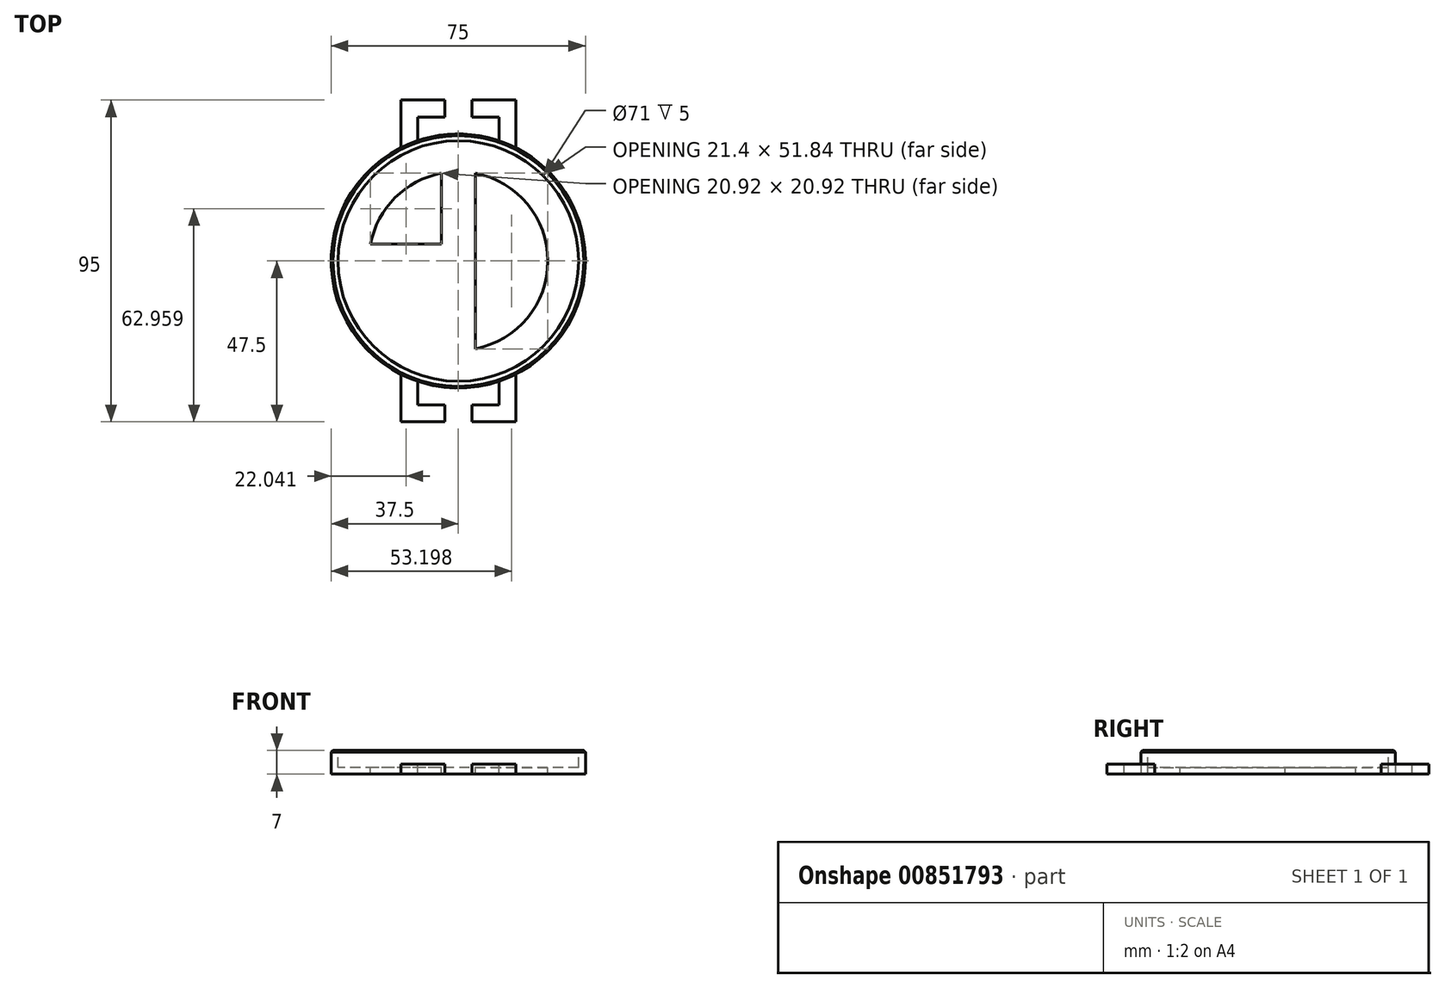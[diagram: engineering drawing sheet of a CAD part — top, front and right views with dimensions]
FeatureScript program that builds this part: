
annotation { "Feature Type Name" : "Feature", "Feature Type Description" : "" }
export const myFeature = defineFeature(function(context is Context, id is Id, definition is map)
    precondition{}
    {
        {
            var Q0;
            Q0=qCreatedBy(makeId("Top.planeOp"),FACE);
            var sketch = newSketch(context, id + "F0", { "sketchPlane" : qUnion([Q0])});
            skCircle(sketch, "E0", {"center": v(0, 0) * mm, "radius": 37.5 * mm});
            skSolve(sketch);
        }
        {
            var Q0;
            Q0=makeQuery(id+"F0.imprint","IMPRINT",FACE,{"disambiguationData":[TD([[makeQuery(id+"F0.imprint","IMPRINT",EDGE,{"derivedFrom":sQuery(id+"F0.wireOp",EDGE,"E0")}),1.0]])]});
            extrude(context, id + "F1", {"entities" : qUnion([Q0]), "depth" : 7 * mm, "offsetDistance" : 25 * mm});
        }
        {
            var Q0;
            Q0=makeQuery(id+"F1.opExtrude","CAP_FACE",FACE,{"disambiguationData":[OSD([sQuery(id+"F0.wireOp",EDGE,"E0")])],"isStart":false});
            var sketch = newSketch(context, id + "F2", { "sketchPlane" : qUnion([Q0])});
            skCircle(sketch, "E1", {"center": v(0, 0) * mm, "radius": 35.5 * mm});
            skSolve(sketch);
        }
        {
            var Q0;
            Q0=makeQuery(id+"F2.imprint","IMPRINT",FACE,{"disambiguationData":[TD([[makeQuery(id+"F2.imprint","IMPRINT",EDGE,{"derivedFrom":sQuery(id+"F2.wireOp",EDGE,"E1")}),1.0]])]});
            extrude(context, id + "F3", {"entities" : qUnion([Q0]), "operationType" : NewBodyOperationType.REMOVE, "oppositeDirection" : true, "depth" : 5 * mm, "offsetDistance" : 25 * mm});
        }
        {
            var Q0;
            Q0=makeQuery(id+"F1.opExtrude","CAP_EDGE",EDGE,{"disambiguationData":[OSD([sQuery(id+"F0.wireOp",EDGE,"E0")])],"isStart":false});
            chamfer(context, id + "F4", {"entities" : qUnion([Q0]), "width" : .5 * mm, "tangentPropagation" : true});
        }
        {
            var Q0;
            Q0=makeQuery(id+"F1.opExtrude","CAP_FACE",FACE,{"disambiguationData":[OSD([sQuery(id+"F0.wireOp",EDGE,"E0")])],"isStart":true});
            var sketch = newSketch(context, id + "F5", { "sketchPlane" : qUnion([Q0])});
            skLineSegment(sketch, "E2", {"start": v(0, 0) * mm, "end": v(0, -47.5) * mm});
            skLineSegment(sketch, "E3", {"start": v(0, 0) * mm, "end": v(0, 47.5) * mm});
            skLineSegment(sketch, "E4", {"start": v(0, 47.5) * mm, "end": v(17, 47.5) * mm});
            skLineSegment(sketch, "E5", {"start": v(0, -47.5) * mm, "end": v(17, -47.5) * mm});
            skLineSegment(sketch, "E6", {"start": v(17, -47.5) * mm, "end": v(17, 47.5) * mm});
            skLineSegment(sketch, "E7", {"start": v(0, 47.5) * mm, "end": v(-17, 47.5) * mm});
            skLineSegment(sketch, "E8", {"start": v(0, -47.5) * mm, "end": v(-17, -47.5) * mm});
            skLineSegment(sketch, "E9", {"start": v(-17, -47.5) * mm, "end": v(-17, 47.5) * mm});
            skSolve(sketch);
        }
        {
            var Q0;
            {var subQ0=sQuery(id+"F5.wireOp",EDGE,"E7");Q0=makeQuery(id+"F5.imprint","IMPRINT",FACE,{"disambiguationData":[TD([[makeQuery(id+"F5.imprint","IMPRINT",EDGE,{"derivedFrom":subQ0}),1.0]])]});}
            var Q1;
            {var subQ0=sQuery(id+"F5.wireOp",EDGE,"E4");Q1=makeQuery(id+"F5.imprint","IMPRINT",FACE,{"disambiguationData":[TD([[makeQuery(id+"F5.imprint","IMPRINT",EDGE,{"derivedFrom":subQ0}),-1.0]])]});}
            var Q2;
            {var subQ0=sQuery(id+"F5.wireOp",EDGE,"E8");Q2=makeQuery(id+"F5.imprint","IMPRINT",FACE,{"disambiguationData":[TD([[makeQuery(id+"F5.imprint","IMPRINT",EDGE,{"derivedFrom":subQ0}),-1.0]])]});}
            var Q3;
            {var subQ0=sQuery(id+"F5.wireOp",EDGE,"E5");Q3=makeQuery(id+"F5.imprint","IMPRINT",FACE,{"disambiguationData":[TD([[makeQuery(id+"F5.imprint","IMPRINT",EDGE,{"derivedFrom":subQ0}),1.0]])]});}
            extrude(context, id + "F6", {"entities" : qUnion([Q0, Q1, Q2, Q3]), "operationType" : NewBodyOperationType.ADD, "depth" : -3 * mm, "offsetDistance" : 25 * mm});
        }
        {
            var Q0;
            Q0=makeQuery(id+"F6.opExtrude","CAP_FACE",FACE,{"disambiguationData":[OSD([sQuery(id+"F0.wireOp",EDGE,"E0"),sQuery(id+"F5.wireOp",EDGE,"E5"),sQuery(id+"F5.wireOp",EDGE,"E6"),sQuery(id+"F5.wireOp",EDGE,"E8"),sQuery(id+"F5.wireOp",EDGE,"E9")])],"isStart":false});
            var sketch = newSketch(context, id + "F7", { "sketchPlane" : qUnion([Q0])});
            skLineSegment(sketch, "E10", {"start": v(0, 47.5) * mm, "end": v(0, 42.5) * mm});
            skLineSegment(sketch, "E11", {"start": v(0, 42.5) * mm, "end": v(17, 42.5) * mm});
            skLineSegment(sketch, "E12", {"start": v(17, 42.5) * mm, "end": v(12, 42.5) * mm});
            skLineSegment(sketch, "E13", {"start": v(12, 42.5) * mm, "end": v(12, 35.53) * mm});
            skLineSegment(sketch, "E14", {"start": v(0, 42.5) * mm, "end": v(-17, 42.5) * mm});
            skLineSegment(sketch, "E15", {"start": v(-17, 42.5) * mm, "end": v(-12, 42.5) * mm});
            skLineSegment(sketch, "E16", {"start": v(-12, 42.5) * mm, "end": v(-12, 35.53) * mm});
            skLineSegment(sketch, "E17", {"start": v(0, 42.5) * mm, "end": v(-4, 42.5) * mm});
            skLineSegment(sketch, "E18", {"start": v(-4, 42.5) * mm, "end": v(4, 42.5) * mm});
            skLineSegment(sketch, "E19", {"start": v(4, 42.5) * mm, "end": v(4, 47.5) * mm});
            skLineSegment(sketch, "E20", {"start": v(-4, 42.5) * mm, "end": v(-4, 47.5) * mm});
            skSolve(sketch);
        }
        {
            var Q0;
            {var subQ3=sQuery(id+"F7.wireOp",EDGE,"E11");Q0=makeQuery(id+"F7.imprint","IMPRINT",FACE,{"disambiguationData":[TD([[makeQuery(id+"F7.imprint","IMPRINT",EDGE,{"derivedFrom":subQ3}),-1.0]])]});}
            var Q1;
            {var subQ0=sQuery(id+"F7.wireOp",EDGE,"E10");Q1=makeQuery(id+"F7.imprint","IMPRINT",FACE,{"disambiguationData":[TD([[makeQuery(id+"F7.imprint","IMPRINT",EDGE,{"derivedFrom":subQ0}),1.0]])]});}
            var Q2;
            {var subQ0=sQuery(id+"F7.wireOp",EDGE,"E10");Q2=makeQuery(id+"F7.imprint","IMPRINT",FACE,{"disambiguationData":[TD([[makeQuery(id+"F7.imprint","IMPRINT",EDGE,{"derivedFrom":subQ0}),-1.0]])]});}
            var Q3;
            {var subQ0=sQuery(id+"F5.wireOp",EDGE,"E9");var subQ1=sQuery(id+"F5.wireOp",EDGE,"E6");var subQ2=sQuery(id+"F0.wireOp",EDGE,"E0");Q3=makeQuery(id+"F6.boolean.opBoolean","MERGE",FACE,{"derivedFrom":[makeQuery(id+"F1.opExtrude","CAP_FACE",FACE,{"disambiguationData":[OSD([subQ2])],"isStart":true}),makeQuery(id+"F6.opExtrude","CAP_FACE",FACE,{"disambiguationData":[OSD([subQ2,sQuery(id+"F5.wireOp",EDGE,"E4"),subQ1,sQuery(id+"F5.wireOp",EDGE,"E7"),subQ0])],"isStart":true}),makeQuery(id+"F6.opExtrude","CAP_FACE",FACE,{"disambiguationData":[OSD([subQ2,sQuery(id+"F5.wireOp",EDGE,"E5"),subQ1,sQuery(id+"F5.wireOp",EDGE,"E8"),subQ0])],"isStart":true})]});}
            extrude(context, id + "F8", {"entities" : qUnion([Q0, Q1, Q2]), "operationType" : NewBodyOperationType.REMOVE, "endBound" : BoundingType.UP_TO_SURFACE, "oppositeDirection" : true, "depth" : 25 * mm, "endBoundEntityFace" : qUnion([Q3]), "offsetDistance" : 25 * mm});
        }
        {
            var Q0;
            Q0=makeQuery(id+"F6.opExtrude","CAP_FACE",FACE,{"disambiguationData":[OSD([sQuery(id+"F0.wireOp",EDGE,"E0"),sQuery(id+"F5.wireOp",EDGE,"E4"),sQuery(id+"F5.wireOp",EDGE,"E6"),sQuery(id+"F5.wireOp",EDGE,"E7"),sQuery(id+"F5.wireOp",EDGE,"E9")])],"isStart":false});
            var sketch = newSketch(context, id + "F9", { "sketchPlane" : qUnion([Q0])});
            skLineSegment(sketch, "E21", {"start": v(0, -47.5) * mm, "end": v(0, -42.5) * mm});
            skLineSegment(sketch, "E22", {"start": v(0, -42.5) * mm, "end": v(-17, -42.5) * mm});
            skLineSegment(sketch, "E23", {"start": v(-17, -42.5) * mm, "end": v(-12, -42.5) * mm});
            skLineSegment(sketch, "E24", {"start": v(-12, -42.5) * mm, "end": v(-12, -35.53) * mm});
            skLineSegment(sketch, "E25", {"start": v(0, -42.5) * mm, "end": v(17, -42.5) * mm});
            skLineSegment(sketch, "E26", {"start": v(17, -42.5) * mm, "end": v(12, -42.5) * mm});
            skLineSegment(sketch, "E27", {"start": v(12, -42.5) * mm, "end": v(12, -35.53) * mm});
            skLineSegment(sketch, "E28", {"start": v(0, -42.5) * mm, "end": v(4, -42.5) * mm});
            skLineSegment(sketch, "E29", {"start": v(4, -42.5) * mm, "end": v(4, -47.5) * mm});
            skLineSegment(sketch, "E30", {"start": v(4, -47.5) * mm, "end": v(-4, -47.5) * mm});
            skLineSegment(sketch, "E31", {"start": v(-4, -47.5) * mm, "end": v(-4, -42.5) * mm});
            skSolve(sketch);
        }
        {
            var Q0;
            {var subQ0=sQuery(id+"F9.wireOp",EDGE,"E24");Q0=makeQuery(id+"F9.imprint","IMPRINT",FACE,{"disambiguationData":[TD([[makeQuery(id+"F9.imprint","IMPRINT",EDGE,{"derivedFrom":subQ0}),-1.0]])]});}
            var Q1;
            {var subQ0=sQuery(id+"F9.wireOp",EDGE,"E21");Q1=makeQuery(id+"F9.imprint","IMPRINT",FACE,{"disambiguationData":[TD([[makeQuery(id+"F9.imprint","IMPRINT",EDGE,{"derivedFrom":subQ0}),-1.0]])]});}
            var Q2;
            {var subQ0=sQuery(id+"F9.wireOp",EDGE,"E21");Q2=makeQuery(id+"F9.imprint","IMPRINT",FACE,{"disambiguationData":[TD([[makeQuery(id+"F9.imprint","IMPRINT",EDGE,{"derivedFrom":subQ0}),1.0]])]});}
            var Q3;
            {var subQ0=sQuery(id+"F5.wireOp",EDGE,"E9");var subQ1=sQuery(id+"F5.wireOp",EDGE,"E6");var subQ2=sQuery(id+"F0.wireOp",EDGE,"E0");Q3=makeQuery(id+"F6.boolean.opBoolean","MERGE",FACE,{"derivedFrom":[makeQuery(id+"F1.opExtrude","CAP_FACE",FACE,{"disambiguationData":[OSD([subQ2])],"isStart":true}),makeQuery(id+"F6.opExtrude","CAP_FACE",FACE,{"disambiguationData":[OSD([subQ2,sQuery(id+"F5.wireOp",EDGE,"E4"),subQ1,sQuery(id+"F5.wireOp",EDGE,"E7"),subQ0])],"isStart":true}),makeQuery(id+"F6.opExtrude","CAP_FACE",FACE,{"disambiguationData":[OSD([subQ2,sQuery(id+"F5.wireOp",EDGE,"E5"),subQ1,sQuery(id+"F5.wireOp",EDGE,"E8"),subQ0])],"isStart":true})]});}
            extrude(context, id + "F10", {"entities" : qUnion([Q0, Q1, Q2]), "operationType" : NewBodyOperationType.REMOVE, "endBound" : BoundingType.UP_TO_SURFACE, "oppositeDirection" : true, "depth" : 25 * mm, "endBoundEntityFace" : qUnion([Q3]), "offsetDistance" : 25 * mm});
        }
        {
            var Q0;
            Q0=makeQuery(id+"F3.boolean.opBoolean","COPY",FACE,{"derivedFrom":makeQuery(id+"F3.opExtrude","CAP_FACE",FACE,{"disambiguationData":[OSD([sQuery(id+"F2.wireOp",EDGE,"E1")])],"isStart":false})});
            var sketch = newSketch(context, id + "F11", { "sketchPlane" : qUnion([Q0])});
            skCircle(sketch, "E32", {"center": v(0, 0) * mm, "radius": 26.4 * mm});
            skLineSegment(sketch, "E33.bottom", {"start": v(5, 28.84) * mm, "end": v(-5, 28.84) * mm});
            skLineSegment(sketch, "E33.top", {"start": v(5, -28.84) * mm, "end": v(-5, -28.84) * mm});
            skLineSegment(sketch, "E33.left", {"start": v(5, 28.84) * mm, "end": v(5, -28.84) * mm});
            skLineSegment(sketch, "E33.right", {"start": v(-5, 28.84) * mm, "end": v(-5, -28.84) * mm});
            skLineSegment(sketch, "E34.bottom", {"start": v(28.92, -5) * mm, "end": v(-28.92, -5) * mm});
            skLineSegment(sketch, "E34.top", {"start": v(28.92, 5) * mm, "end": v(-28.92, 5) * mm});
            skLineSegment(sketch, "E34.left", {"start": v(28.92, -5) * mm, "end": v(28.92, 5) * mm});
            skLineSegment(sketch, "E34.right", {"start": v(-28.92, -5) * mm, "end": v(-28.92, 5) * mm});
            skSolve(sketch);
        }
        {
            var Q0;
            {var subQ0=sQuery(id+"F11.wireOp",EDGE,"E33.left");var subQ1=sQuery(id+"F11.wireOp",EDGE,"E32");var subQ2=makeQuery(id+"F11.imprint","INTERSECT",VERTEX,{"disambiguationData":[OD(0.0)],"derivedFrom":[subQ1,subQ0]});Q0=makeQuery(id+"F11.imprint","IMPRINT",FACE,{"disambiguationData":[TD([[makeQuery(id+"F11.imprint","IMPRINT",EDGE,{"disambiguationData":[TD([[subQ2,1.0]])],"derivedFrom":subQ1}),1.0]])]});}
            var Q1;
            {var subQ0=sQuery(id+"F11.wireOp",EDGE,"E33.right");var subQ1=sQuery(id+"F11.wireOp",EDGE,"E32");var subQ2=makeQuery(id+"F11.imprint","INTERSECT",VERTEX,{"disambiguationData":[OD(0.0)],"derivedFrom":[subQ1,subQ0]});Q1=makeQuery(id+"F11.imprint","IMPRINT",FACE,{"disambiguationData":[TD([[makeQuery(id+"F11.imprint","IMPRINT",EDGE,{"disambiguationData":[TD([[subQ2,-1.0]])],"derivedFrom":subQ1}),1.0]])]});}
            var Q2;
            {var subQ0=sQuery(id+"F11.wireOp",EDGE,"E33.left");var subQ1=sQuery(id+"F11.wireOp",EDGE,"E32");var subQ2=makeQuery(id+"F11.imprint","INTERSECT",VERTEX,{"disambiguationData":[OD(1.0)],"derivedFrom":[subQ1,subQ0]});Q2=makeQuery(id+"F11.imprint","IMPRINT",FACE,{"disambiguationData":[TD([[makeQuery(id+"F11.imprint","IMPRINT",EDGE,{"disambiguationData":[TD([[subQ2,-1.0]])],"derivedFrom":subQ1}),1.0]])]});}
            var Q3;
            {var subQ0=sQuery(id+"F11.wireOp",EDGE,"E34.bottom");var subQ1=sQuery(id+"F11.wireOp",EDGE,"E32");var subQ2=makeQuery(id+"F11.imprint","INTERSECT",VERTEX,{"disambiguationData":[OD(0.0)],"derivedFrom":[subQ1,subQ0]});Q3=makeQuery(id+"F11.imprint","IMPRINT",FACE,{"disambiguationData":[TD([[makeQuery(id+"F11.imprint","IMPRINT",EDGE,{"disambiguationData":[TD([[subQ2,-1.0]])],"derivedFrom":subQ1}),1.0]])]});}
            var Q4;
            {var subQ0=sQuery(id+"F5.wireOp",EDGE,"E9");var subQ1=sQuery(id+"F5.wireOp",EDGE,"E6");var subQ2=sQuery(id+"F0.wireOp",EDGE,"E0");Q4=makeQuery(id+"F6.boolean.opBoolean","MERGE",FACE,{"derivedFrom":[makeQuery(id+"F1.opExtrude","CAP_FACE",FACE,{"disambiguationData":[OSD([subQ2])],"isStart":true}),makeQuery(id+"F6.opExtrude","CAP_FACE",FACE,{"disambiguationData":[OSD([subQ2,sQuery(id+"F5.wireOp",EDGE,"E4"),subQ1,sQuery(id+"F5.wireOp",EDGE,"E7"),subQ0])],"isStart":true}),makeQuery(id+"F6.opExtrude","CAP_FACE",FACE,{"disambiguationData":[OSD([subQ2,sQuery(id+"F5.wireOp",EDGE,"E5"),subQ1,sQuery(id+"F5.wireOp",EDGE,"E8"),subQ0])],"isStart":true})]});}
            extrude(context, id + "F12", {"entities" : qUnion([Q0, Q1, Q2, Q3]), "operationType" : NewBodyOperationType.REMOVE, "endBound" : BoundingType.UP_TO_SURFACE, "oppositeDirection" : true, "depth" : 25 * mm, "endBoundEntityFace" : qUnion([Q4]), "offsetDistance" : 25 * mm});
        }
    });
